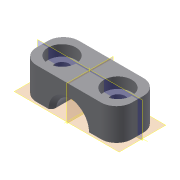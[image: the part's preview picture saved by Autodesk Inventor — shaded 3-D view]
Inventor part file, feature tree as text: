
AUTODESK INVENTOR PART (.ipt)
format: ipt  version: 2015 SP2 (Build 190223200, 223)  size: 134,656 bytes
history: native  units: mm
features: extrude x3, sketch x3, hole x2, fillet x2, other x1, chamfer x1
ambient origin geometry x8: Origin, YZ Plane, XZ Plane, XY Plane, X Axis, Y Axis, Z Axis, Center Point
bodies: Body1 (feature_tree)
feature tree (12):
  other  "Sólido1"
  extrude  "Extrusión1"  Depth=11.0mm
  extrude  "Extrusión2"  Depth=7.2mm
  hole  "Agujero1"  [1 undecoded]
  hole  "Agujero2"  [1 undecoded]
  fillet  "Empalme1"  Radius=2.79mm
  extrude  "Extrusión3"  Depth=10.0mm
  chamfer  "Chaflán1"  Distance=4.0mm
  fillet  "Empalme2"  Radius=4.25mm
  sketch  "Boceto1"  dims[d0=24.75mm d1=11.0mm]
  sketch  "Boceto2"  dims[d2=8.25mm d3=0.0mm d4=7.2mm]
  sketch  "Boceto3"  dims[d5=7.2mm d6=7.3mm d7=7.25mm d10=2.79mm d11=0.0mm d21=10.0mm d22=10.0mm d14=3.78mm d15=6.0mm d16=4.0mm d17=2.0mm d18=90.0deg d19=8.0mm d20=20.594885mm d23=10.0mm d24=10.0mm d25=3.78mm d26=6.0mm d27=4.0mm d28=2.0mm d29=90.0deg d30=8.0mm d31=20.594885mm d32=4.0mm d34=4.25mm d35=2.79mm d36=0.0mm d37=0.5mm d38=1.0mm d39=2.0mm d40=45.0deg]
note: 2 required parameter values undecoded (feature->parameter linkage not recoverable at this tier; creation-order binding heuristic only, values carry confidence <= 0.55)
